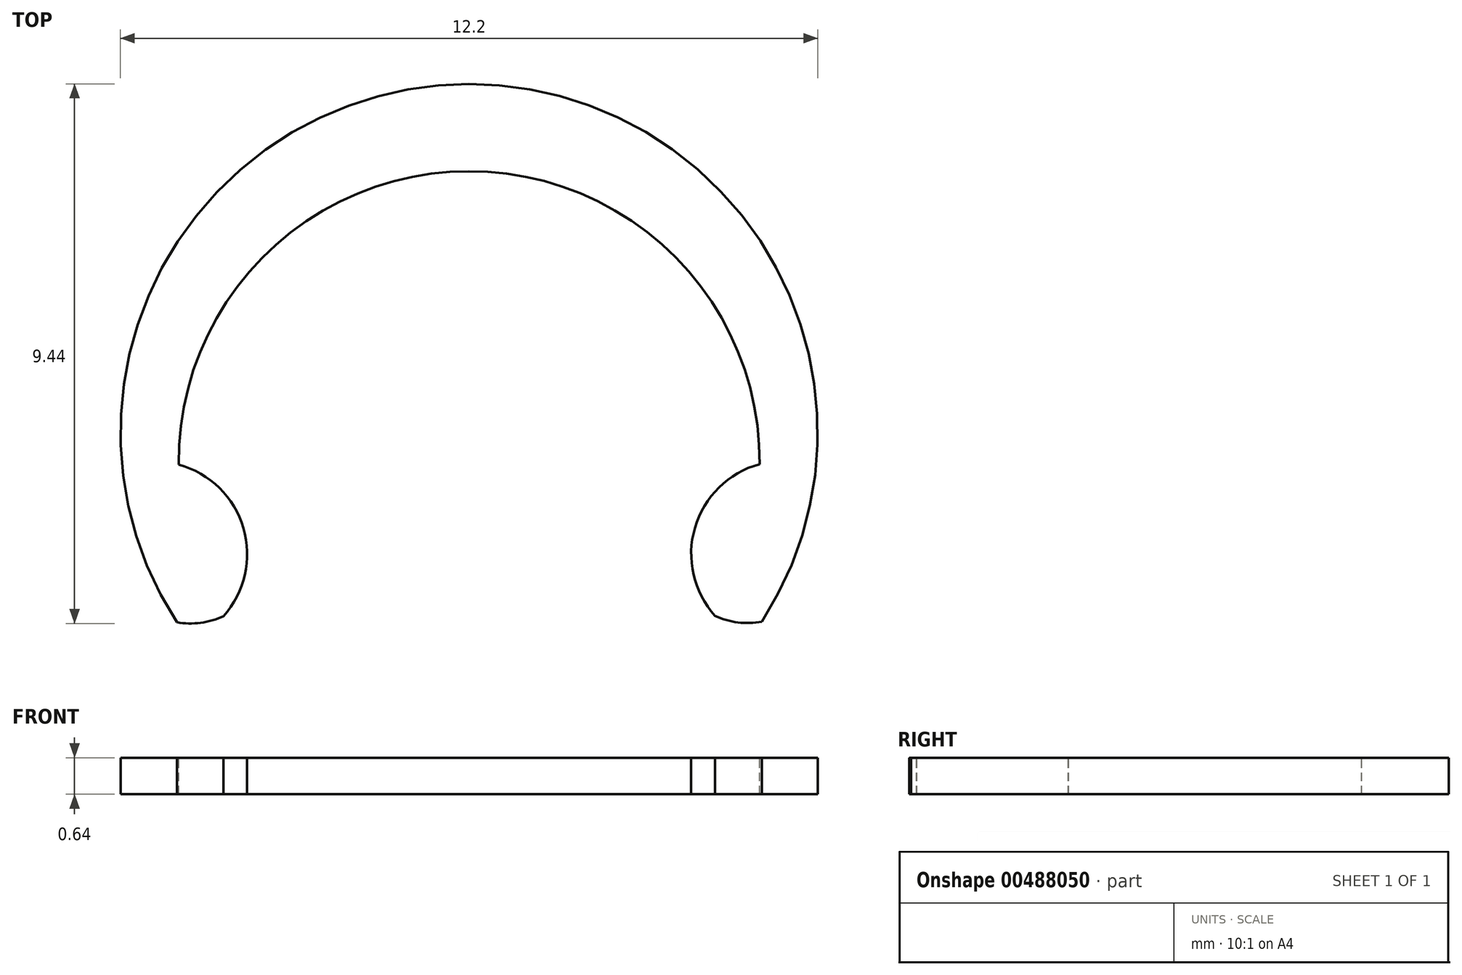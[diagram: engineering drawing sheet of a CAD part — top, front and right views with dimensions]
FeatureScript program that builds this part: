
annotation { "Feature Type Name" : "Feature", "Feature Type Description" : "" }
export const myFeature = defineFeature(function(context is Context, id is Id, definition is map)
    precondition{}
    {
        {
            var Q0;
            Q0=qCreatedBy(makeId("Top.planeOp"),FACE);
            var sketch = newSketch(context, id + "F0", { "sketchPlane" : qUnion([Q0])});
            skCircle(sketch, "E0", {"center": v(0, 0) * mm, "radius": 6.1 * mm});
            skSolve(sketch);
        }
        {
            var Q0;
            Q0 = qSketchRegion(id + "F0", true);
            extrude(context, id + "F1", {"entities" : qUnion([Q0]), "depth" : 0.64 * mm, "offsetDistance" : 25.4 * mm});
        }
        {
            var Q0;
            Q0=makeQuery(id+"F1.opExtrude","CAP_FACE",FACE,{"disambiguationData":[OSD([sQuery(id+"F0.wireOp",EDGE,"E0")])],"isStart":false});
            var sketch = newSketch(context, id + "F2", { "sketchPlane" : qUnion([Q0])});
            skCircle(sketch, "E1", {"center": v(0, -0.5) * mm, "radius": 5.08 * mm});
            skCircle(sketch, "E2", {"center": v(4.88, -1.94) * mm, "radius": 1.4 * mm});
            skCircle(sketch, "E3", {"center": v(-4.87, -1.94) * mm, "radius": 1.4 * mm});
            skLineSegment(sketch, "E4", {"start": v(-5.07, -0.27) * mm, "end": v(-6.1, -0.27) * mm, "construction": true});
            skLineSegment(sketch, "E5", {"start": v(0, 6.1) * mm, "end": v(0, -6.1) * mm, "construction": true});
            skLineSegment(sketch, "E6", {"start": v(5.07, -0.27) * mm, "end": v(6.1, -0.27) * mm, "construction": true});
            skArc(sketch, "E7", {"start": v(-4.3, -3.22) * mm, "mid": v(-3.95, -1.67) * mm, "end": v(-5.08, -0.56) * mm});
            skArc(sketch, "E8", {"start": v(5.08, -0.55) * mm, "mid": v(3.95, -1.66) * mm, "end": v(4.3, -3.2) * mm});
            skSolve(sketch);
        }
        {
            var Q0;
            {var subQ0=sQuery(id+"F2.wireOp",EDGE,"E2");var subQ1=makeQuery(id+"F1.opExtrude","CAP_EDGE",EDGE,{"disambiguationData":[OSD([sQuery(id+"F0.wireOp",EDGE,"E0")])],"isStart":false});var subQ2=makeQuery(id+"F2.imprint","INTERSECT",VERTEX,{"disambiguationData":[OD(0.0)],"derivedFrom":[subQ1,subQ0]});Q0=makeQuery(id+"F2.imprint","IMPRINT",FACE,{"disambiguationData":[TD([[makeQuery(id+"F2.imprint","IMPRINT",EDGE,{"disambiguationData":[TD([[subQ2,1.0]])],"derivedFrom":subQ0}),1.0]])]});}
            var Q1;
            {var subQ0=sQuery(id+"F2.wireOp",EDGE,"E3");var subQ1=makeQuery(id+"F1.opExtrude","CAP_EDGE",EDGE,{"disambiguationData":[OSD([sQuery(id+"F0.wireOp",EDGE,"E0")])],"isStart":false});var subQ2=makeQuery(id+"F2.imprint","INTERSECT",VERTEX,{"disambiguationData":[OD(0.0)],"derivedFrom":[subQ1,subQ0]});Q1=makeQuery(id+"F2.imprint","IMPRINT",FACE,{"disambiguationData":[TD([[makeQuery(id+"F2.imprint","IMPRINT",EDGE,{"disambiguationData":[TD([[subQ2,-1.0]])],"derivedFrom":subQ0}),1.0]])]});}
            var Q2;
            {var subQ1=sQuery(id+"F2.wireOp",EDGE,"E1");var subQ5=sQuery(id+"F2.wireOp",EDGE,"jYk9UhXr-IrjS-Rj9X-mbA1-QcFR8c5SNirz");var subQ6=makeQuery(id+"F2.imprint","INTERSECT",VERTEX,{"disambiguationData":[OD(0.0)],"derivedFrom":[subQ1,subQ5]});Q2=makeQuery(id+"F2.imprint","IMPRINT",FACE,{"disambiguationData":[TD([[makeQuery(id+"F2.imprint","IMPRINT",EDGE,{"disambiguationData":[TD([[subQ6,1.0]])],"derivedFrom":subQ1}),1.0]])]});}
            var Q3;
            {var subQ0=sQuery(id+"F2.wireOp",EDGE,"ZS2QDb2g-kdQr-1Kkx-KukY-WNXZo9YZ2ozh");var subQ1=sQuery(id+"F2.wireOp",EDGE,"E1");var subQ2=makeQuery(id+"F2.imprint","INTERSECT",VERTEX,{"disambiguationData":[OD(0.0)],"derivedFrom":[subQ1,subQ0]});Q3=makeQuery(id+"F2.imprint","IMPRINT",FACE,{"disambiguationData":[TD([[makeQuery(id+"F2.imprint","IMPRINT",EDGE,{"disambiguationData":[TD([[subQ2,1.0]])],"derivedFrom":subQ1}),1.0]])]});}
            var Q4;
            {var subQ0=sQuery(id+"F2.wireOp",EDGE,"jYk9UhXr-IrjS-Rj9X-mbA1-QcFR8c5SNirz");var subQ1=sQuery(id+"F2.wireOp",EDGE,"E1");var subQ2=makeQuery(id+"F2.imprint","INTERSECT",VERTEX,{"disambiguationData":[OD(0.0)],"derivedFrom":[subQ1,subQ0]});Q4=makeQuery(id+"F2.imprint","IMPRINT",FACE,{"disambiguationData":[TD([[makeQuery(id+"F2.imprint","IMPRINT",EDGE,{"disambiguationData":[TD([[subQ2,-1.0]])],"derivedFrom":subQ1}),1.0]])]});}
            var Q5;
            {var subQ0=sQuery(id+"F2.wireOp",EDGE,"E7");var subQ1=sQuery(id+"F2.wireOp",EDGE,"E3");var subQ2=sQuery(id+"F2.wireOp",EDGE,"E1");var subQ3=makeQuery(id+"F2.imprint","INTERSECT",VERTEX,{"disambiguationData":[OD(0.0)],"derivedFrom":[subQ2,subQ1,subQ0]});Q5=makeQuery(id+"F2.imprint","IMPRINT",FACE,{"disambiguationData":[TD([[makeQuery(id+"F2.imprint","IMPRINT",EDGE,{"disambiguationData":[TD([[subQ3,-1.0]])],"derivedFrom":subQ2}),1.0]])]});}
            var Q6;
            {var subQ0=sQuery(id+"F2.wireOp",EDGE,"E7");Q6=makeQuery(id+"F2.imprint","IMPRINT",FACE,{"disambiguationData":[TD([[makeQuery(id+"F2.imprint","IMPRINT",EDGE,{"derivedFrom":subQ0}),-1.0]])]});}
            var Q7;
            {var subQ0=sQuery(id+"F2.wireOp",EDGE,"E8");Q7=makeQuery(id+"F2.imprint","IMPRINT",FACE,{"disambiguationData":[TD([[makeQuery(id+"F2.imprint","IMPRINT",EDGE,{"derivedFrom":subQ0}),-1.0]])]});}
            var Q8;
            {var subQ3=sQuery(id+"F2.wireOp",EDGE,"E2");var subQ5=makeQuery(id+"F1.opExtrude","CAP_EDGE",EDGE,{"disambiguationData":[OSD([sQuery(id+"F0.wireOp",EDGE,"E0")])],"isStart":false});var subQ6=makeQuery(id+"F2.imprint","INTERSECT",VERTEX,{"disambiguationData":[OD(1.0)],"derivedFrom":[subQ5,subQ3]});Q8=makeQuery(id+"F2.imprint","IMPRINT",FACE,{"disambiguationData":[TD([[makeQuery(id+"F2.imprint","IMPRINT",EDGE,{"disambiguationData":[TD([[subQ6,1.0]])],"derivedFrom":subQ5}),1.0]])]});}
            extrude(context, id + "F3", {"entities" : qUnion([Q0, Q1, Q2, Q3, Q4, Q5, Q6, Q7, Q8]), "operationType" : NewBodyOperationType.REMOVE, "oppositeDirection" : true, "depth" : 25.4 * mm, "offsetDistance" : 25.4 * mm});
        }
    });
